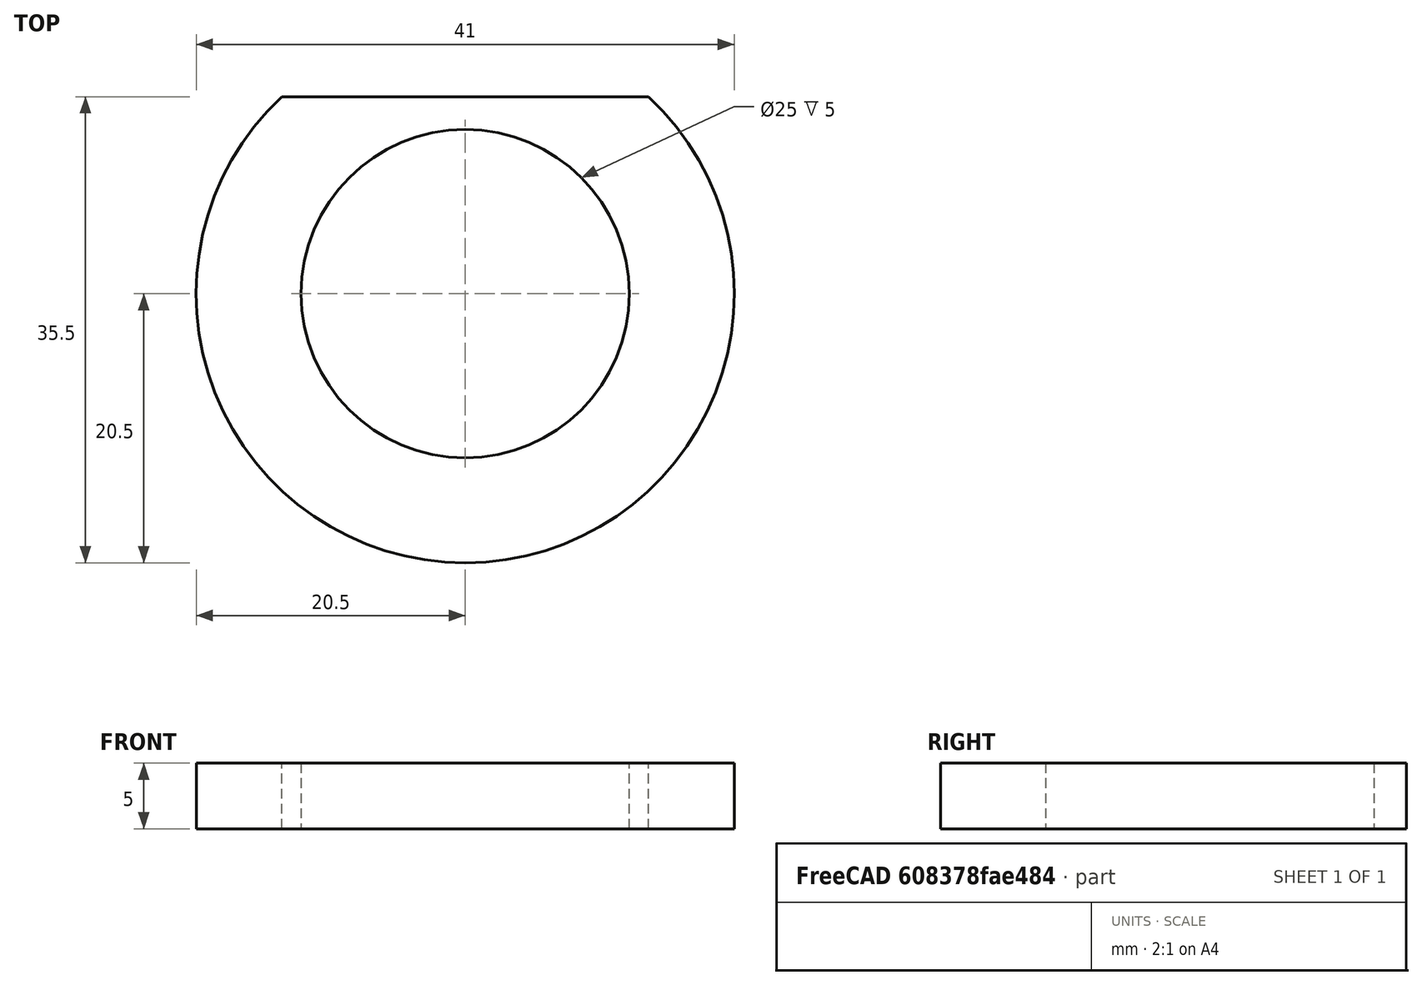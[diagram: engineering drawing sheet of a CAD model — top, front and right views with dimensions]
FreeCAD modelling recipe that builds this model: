
FCSTD DOCUMENT  (FreeCAD 0.16R6706 (Git))
Label: iROB-EA_Soporte_Motores_B
License: All rights reserved
LicenseURL: http://en.wikipedia.org/wiki/All_rights_reserved
objects: Sketcher::SketchObject×1, PartDesign::Pad×1
note: 3 computed .brp shape members not serialized (recipe doc carries the construction recipe); baked Part::Feature solids carry a one-line shape summary decoded from their .brp

FEATURE [Sketcher::SketchObject] Sketch  label="Base"
  sketch-geometry (4):
    g0: Circle CenterX=0 CenterY=0 CenterZ=0 NormalX=0 NormalY=0 NormalZ=1 Radius=12.5
    g1: ArcOfCircle CenterX=0 CenterY=0 CenterZ=0 NormalX=0 NormalY=0 NormalZ=1 Radius=20.5 StartAngle=2.32077 EndAngle=7.10401
    g2: LineSegment StartX=-13.9732 StartY=15 StartZ=0 EndX=13.9732 EndY=15 EndZ=0
    g3: LineSegment [constr] StartX=0 StartY=15 StartZ=0 EndX=0 EndY=0 EndZ=0
  constraints (11):
    c: Radius(g0) = 12.5
    c: Radius(g1) = 20.5
    c: Coincident(g1,g0)
    c: Coincident(g0,g-1)
    c: Horizontal(g2)
    c: Vertical(g3)
    c: Coincident(g3,g-1)
    c: PointOnObject(g3,g2)
    c: DistanceY(g3,g3) = 15
    c: Coincident(g1,g2)
    c: Coincident(g1,g2)
FEATURE [PartDesign::Pad] Pad
  Length = 5
  Length2 = 100
  Sketch = -> Sketch
  Type = 0
